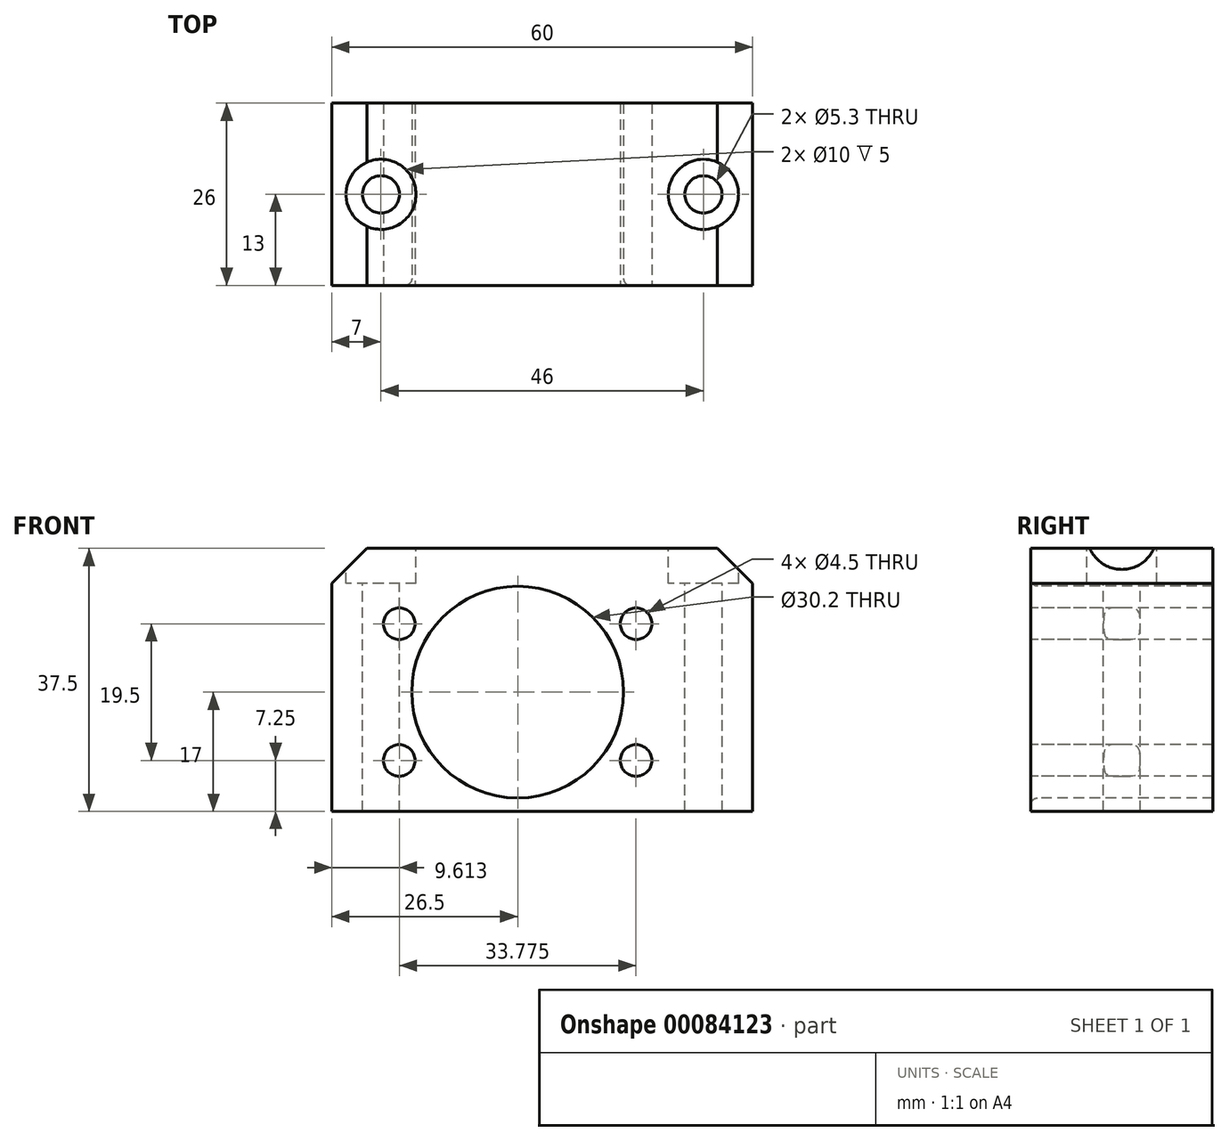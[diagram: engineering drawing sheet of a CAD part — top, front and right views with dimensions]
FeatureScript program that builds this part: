
annotation { "Feature Type Name" : "Feature", "Feature Type Description" : "" }
export const myFeature = defineFeature(function(context is Context, id is Id, definition is map)
    precondition{}
    {
        {
            var Q0;
            Q0=qCreatedBy(makeId("Front.planeOp"),FACE);
            var sketch = newSketch(context, id + "F0", { "sketchPlane" : qUnion([Q0])});
            skLineSegment(sketch, "E0.bottom", {"start": v(30, -17.5) * mm, "end": v(-30, -17.5) * mm});
            skLineSegment(sketch, "E0.top", {"start": v(30, 20) * mm, "end": v(-30, 20) * mm});
            skLineSegment(sketch, "E0.left", {"start": v(30, -17.5) * mm, "end": v(30, 20) * mm});
            skLineSegment(sketch, "E0.right", {"start": v(-30, -17.5) * mm, "end": v(-30, 20) * mm});
            skPoint(sketch, "E0.middle", {"position": v(0, 1.25) * mm});
            skLineSegment(sketch, "E1", {"start": v(-31, 0) * mm, "end": v(29, 0) * mm, "construction": true});
            skLineSegment(sketch, "E2", {"start": v(0, 20) * mm, "end": v(0, -17.5) * mm, "construction": true});
            skCircle(sketch, "E3", {"center": v(-3.5, -0.5) * mm, "radius": 15.1 * mm});
            skCircle(sketch, "E4", {"center": v(-3.5, -0.5) * mm, "radius": 19.5 * mm, "construction": true});
            skLineSegment(sketch, "E5", {"start": v(-3.5, -0.5) * mm, "end": v(13.39, 9.25) * mm, "construction": true});
            skCircle(sketch, "E6", {"center": v(13.39, 9.25) * mm, "radius": 2.25 * mm});
            skLineSegment(sketch, "E7", {"start": v(-3.5, -0.5) * mm, "end": v(-3.5, -17.5) * mm, "construction": true});
            skLineSegment(sketch, "E8", {"start": v(-3.5, -0.5) * mm, "end": v(30, -0.5) * mm, "construction": true});
            skCircle(sketch, "E9.MirrorC", {"center": v(-20.39, 9.25) * mm, "radius": 2.25 * mm});
            skCircle(sketch, "E10.MirrorC", {"center": v(13.39, -10.25) * mm, "radius": 2.25 * mm});
            skCircle(sketch, "E11.MirrorC", {"center": v(-20.39, -10.25) * mm, "radius": 2.25 * mm});
            skSolve(sketch);
        }
        {
            var Q0;
            Q0=makeQuery(id+"F0.imprint","IMPRINT",FACE,{"disambiguationData":[TD([[makeQuery(id+"F0.imprint","IMPRINT",EDGE,{"derivedFrom":sQuery(id+"F0.wireOp",EDGE,"E0.bottom")}),-1.0]])]});
            extrude(context, id + "F1", {"entities" : qUnion([Q0]), "oppositeDirection" : true, "depth" : 26 * mm});
        }
        {
            var Q0;
            Q0=makeQuery(id+"F1.opExtrude","SWEPT_FACE",FACE,{"disambiguationData":[OSD([sQuery(id+"F0.wireOp",EDGE,"E0.top")])]});
            var sketch = newSketch(context, id + "F2", { "sketchPlane" : qUnion([Q0])});
            skLineSegment(sketch, "E12", {"start": v(-30, 13) * mm, "end": v(30, 13) * mm, "construction": true});
            skLineSegment(sketch, "E13", {"start": v(0, 26) * mm, "end": v(0, 0) * mm, "construction": true});
            skPoint(sketch, "E14", {"position": v(-23, 13) * mm});
            skPoint(sketch, "E15.MirrorP", {"position": v(23, 13) * mm});
            skSolve(sketch);
        }
        {
            var Q0;
            Q0=sQuery(id+"F2.wireOp",VERTEX,"E14");
            var Q1;
            Q1=sQuery(id+"F2.wireOp",VERTEX,"E15.MirrorP");
            var Q2;
            Q2=makeQuery(id+"F1.opExtrude","SWEPT_BODY",BODY,{"disambiguationData":[OSD([sQuery(id+"F0.wireOp",EDGE,"E0.bottom"),sQuery(id+"F0.wireOp",EDGE,"E0.top"),sQuery(id+"F0.wireOp",EDGE,"E0.left"),sQuery(id+"F0.wireOp",EDGE,"E0.right"),sQuery(id+"F0.wireOp",EDGE,"E3"),sQuery(id+"F0.wireOp",EDGE,"E6"),sQuery(id+"F0.wireOp",EDGE,"f66d2163-7695-42a6-96f9-d8294fbb344c0.MirrorC"),sQuery(id+"F0.wireOp",EDGE,"1c4fe97c-1c87-4d79-8416-8439dd114edd0.MirrorC"),sQuery(id+"F0.wireOp",EDGE,"38c68ae6-5161-4924-9519-811901cb42380.MirrorC")])]});
            hole(context, id + "F3", {"style" : HoleStyle.C_BORE, "endStyle" : HoleEndStyle.THROUGH, "holeDiameter" : 5.3 * mm, "cBoreDiameter" : 10 * mm, "cBoreDepth" : 5 * mm, "isTappedThrough" : true, "tappedDepth" : 12 * mm, "tapClearance" : 3, "startFromSketch" : true, "locations" : qUnion([Q0, Q1]), "scope" : qUnion([Q2])});
        }
        {
            var Q0;
            Q0=makeQuery(id+"F1.opExtrude","SWEPT_EDGE",EDGE,{"disambiguationData":[OSD([sQuery(id+"F0.wireOp",EDGE,"E0.top"),sQuery(id+"F0.wireOp",EDGE,"E0.right")])]});
            var Q1;
            Q1=makeQuery(id+"F1.opExtrude","SWEPT_EDGE",EDGE,{"disambiguationData":[OSD([sQuery(id+"F0.wireOp",EDGE,"E0.top"),sQuery(id+"F0.wireOp",EDGE,"E0.left")])]});
            chamfer(context, id + "F4", {"entities" : qUnion([Q0, Q1]), "width" : 5 * mm, "tangentPropagation" : true});
        }
        {
            var Q0;
            Q0=makeQuery(id+"F1.opExtrude","CAP_EDGE",EDGE,{"disambiguationData":[OSD([sQuery(id+"F0.wireOp",EDGE,"E3")])],"isStart":true});
            fillet(context, id + "F5", {"entities" : qUnion([Q0]), "radius" : 1 * mm, "tangentPropagation" : true, "allowEdgeOverflow" : false});
        }
    });
